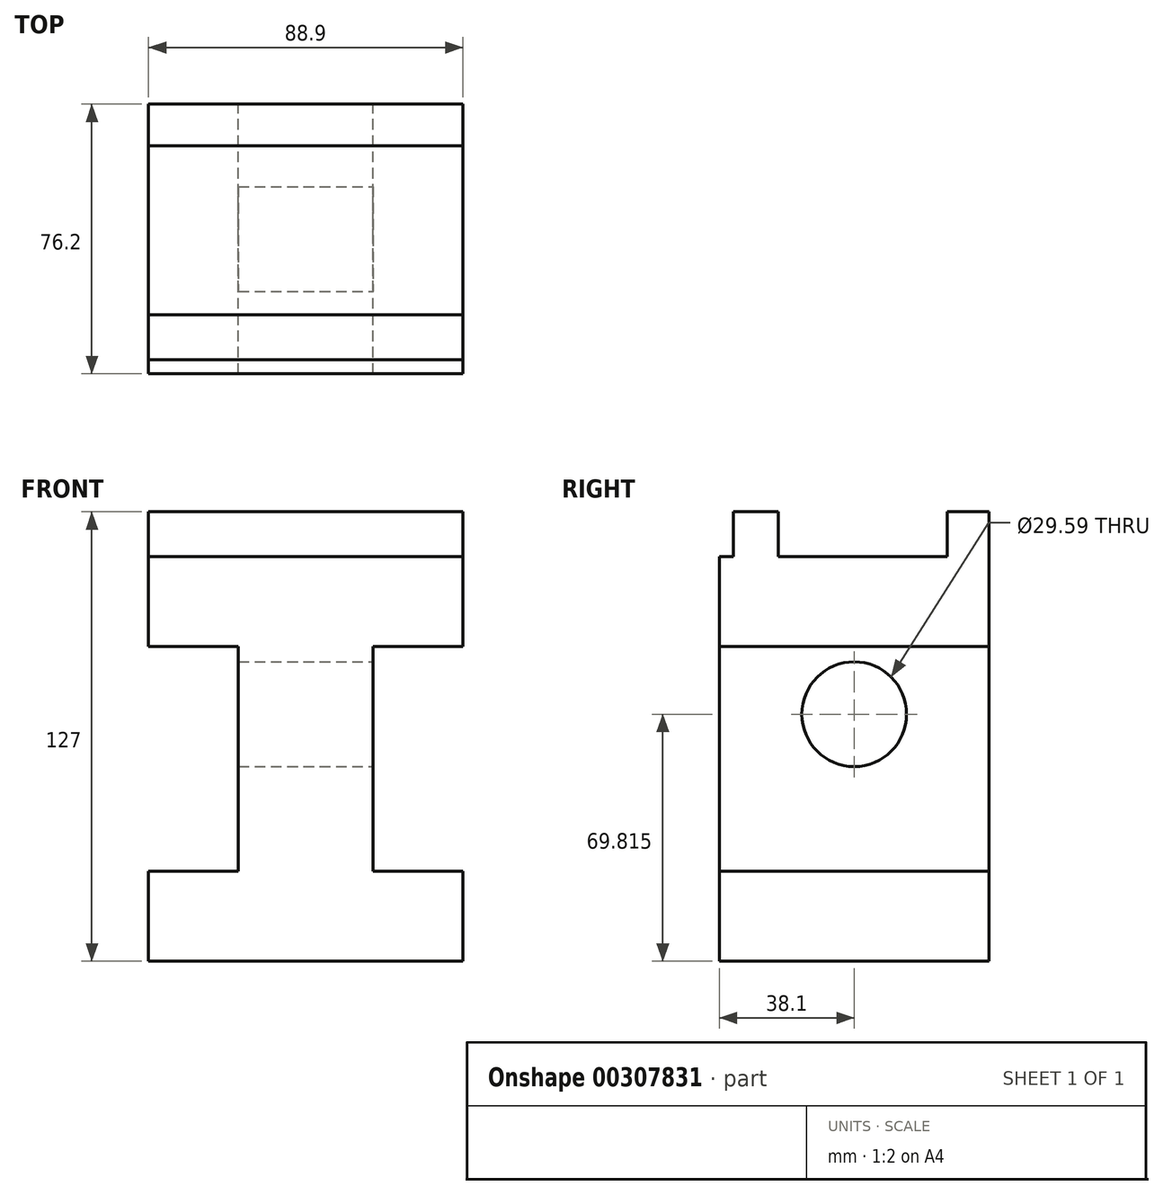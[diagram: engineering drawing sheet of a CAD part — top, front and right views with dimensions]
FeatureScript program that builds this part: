
annotation { "Feature Type Name" : "Feature", "Feature Type Description" : "" }
export const myFeature = defineFeature(function(context is Context, id is Id, definition is map)
    precondition{}
    {
        {
            var Q0;
            Q0=qCreatedBy(makeId("Front.planeOp"),FACE);
            var sketch = newSketch(context, id + "F0", { "sketchPlane" : qUnion([Q0])});
            skLineSegment(sketch, "E0", {"start": v(42.44, -26.06) * mm, "end": v(-46.46, -26.06) * mm});
            skLineSegment(sketch, "E1", {"start": v(42.44, -26.06) * mm, "end": v(42.44, -0.66) * mm});
            skLineSegment(sketch, "E2", {"start": v(42.44, -0.66) * mm, "end": v(17.04, -0.66) * mm});
            skLineSegment(sketch, "E3", {"start": v(17.04, -0.66) * mm, "end": v(17.04, 62.84) * mm});
            skLineSegment(sketch, "E4", {"start": v(17.04, 62.84) * mm, "end": v(42.44, 62.84) * mm});
            skLineSegment(sketch, "E5", {"start": v(42.44, 62.84) * mm, "end": v(42.44, 88.24) * mm});
            skLineSegment(sketch, "E6", {"start": v(42.44, 88.24) * mm, "end": v(-46.46, 88.24) * mm});
            skLineSegment(sketch, "E7", {"start": v(-46.46, 88.24) * mm, "end": v(-46.46, 62.84) * mm});
            skLineSegment(sketch, "E8", {"start": v(-46.46, 62.84) * mm, "end": v(-21.06, 62.84) * mm});
            skLineSegment(sketch, "E9", {"start": v(-21.06, 62.84) * mm, "end": v(-21.06, -0.66) * mm});
            skLineSegment(sketch, "E10", {"start": v(-21.06, -0.66) * mm, "end": v(-46.46, -0.66) * mm});
            skLineSegment(sketch, "E11", {"start": v(-46.46, -0.66) * mm, "end": v(-46.46, -26.06) * mm});
            skSolve(sketch);
        }
        {
            var Q0;
            {var subQ0=sQuery(id+"F0.wireOp",EDGE,"E1");Q0=makeQuery(id+"F0.imprint","IMPRINT",FACE,{"disambiguationData":[TD([[makeQuery(id+"F0.imprint","IMPRINT",EDGE,{"derivedFrom":subQ0}),1.0]])]});}
            extrude(context, id + "F1", {"entities" : qUnion([Q0]), "depth" : 76.2 * mm});
        }
        {
            var Q0;
            Q0=makeQuery(id+"F1.opExtrude","SWEPT_FACE",FACE,{"disambiguationData":[OSD([sQuery(id+"F0.wireOp",EDGE,"E3")])]});
            var sketch = newSketch(context, id + "F2", { "sketchPlane" : qUnion([Q0])});
            skLineSegment(sketch, "E12", {"start": v(0, 43.75) * mm, "end": v(-38.1, 43.75) * mm});
            skPoint(sketch, "E12.endSnap0", {"position": v(-38.1, 62.84) * mm});
            skCircle(sketch, "E13", {"center": v(-38.1, 43.75) * mm, "radius": 14.8 * mm});
            skSolve(sketch);
        }
        {
            var Q0;
            Q0=makeQuery(id+"F2.imprint","IMPRINT",FACE,{"disambiguationData":[TD([[makeQuery(id+"F2.imprint","IMPRINT",EDGE,{"derivedFrom":sQuery(id+"F2.wireOp",EDGE,"E13")}),1.0]])]});
            extrude(context, id + "F3", {"entities" : qUnion([Q0]), "operationType" : NewBodyOperationType.REMOVE, "oppositeDirection" : true, "depth" : 127 * mm});
        }
        {
            var Q0;
            Q0=makeQuery(id+"F1.opExtrude","SWEPT_FACE",FACE,{"disambiguationData":[OSD([sQuery(id+"F0.wireOp",EDGE,"E6")])]});
            var sketch = newSketch(context, id + "F4", { "sketchPlane" : qUnion([Q0])});
            skLineSegment(sketch, "E14.bottom", {"start": v(-46.46, 0.93) * mm, "end": v(42.44, 0.93) * mm});
            skLineSegment(sketch, "E14.top", {"start": v(-46.46, -11.77) * mm, "end": v(42.44, -11.77) * mm});
            skLineSegment(sketch, "E14.left", {"start": v(-46.46, 0.93) * mm, "end": v(-46.46, -11.77) * mm});
            skLineSegment(sketch, "E14.right", {"start": v(42.44, 0.93) * mm, "end": v(42.44, -11.77) * mm});
            skLineSegment(sketch, "E15.bottom", {"start": v(-46.46, -72.23) * mm, "end": v(42.44, -72.23) * mm});
            skLineSegment(sketch, "E15.top", {"start": v(-46.46, -59.53) * mm, "end": v(42.44, -59.53) * mm});
            skLineSegment(sketch, "E15.left", {"start": v(-46.46, -72.23) * mm, "end": v(-46.46, -59.53) * mm});
            skLineSegment(sketch, "E15.right", {"start": v(42.44, -72.23) * mm, "end": v(42.44, -59.53) * mm});
            skSolve(sketch);
        }
        {
            var Q0;
            {var subQ0=sQuery(id+"F4.wireOp",EDGE,"E14.top");Q0=makeQuery(id+"F4.imprint","IMPRINT",FACE,{"disambiguationData":[TD([[makeQuery(id+"F4.imprint","IMPRINT",EDGE,{"derivedFrom":subQ0}),1.0]])]});}
            extrude(context, id + "F5", {"entities" : qUnion([Q0]), "operationType" : NewBodyOperationType.ADD, "depth" : 12.7 * mm});
        }
        {
            var Q0;
            Q0=makeQuery(id+"F4.imprint","IMPRINT",FACE,{"disambiguationData":[TD([[makeQuery(id+"F4.imprint","IMPRINT",EDGE,{"derivedFrom":sQuery(id+"F4.wireOp",EDGE,"E15.bottom")}),1.0]])]});
            extrude(context, id + "F6", {"entities" : qUnion([Q0]), "operationType" : NewBodyOperationType.ADD, "depth" : 12.7 * mm});
        }
    });
